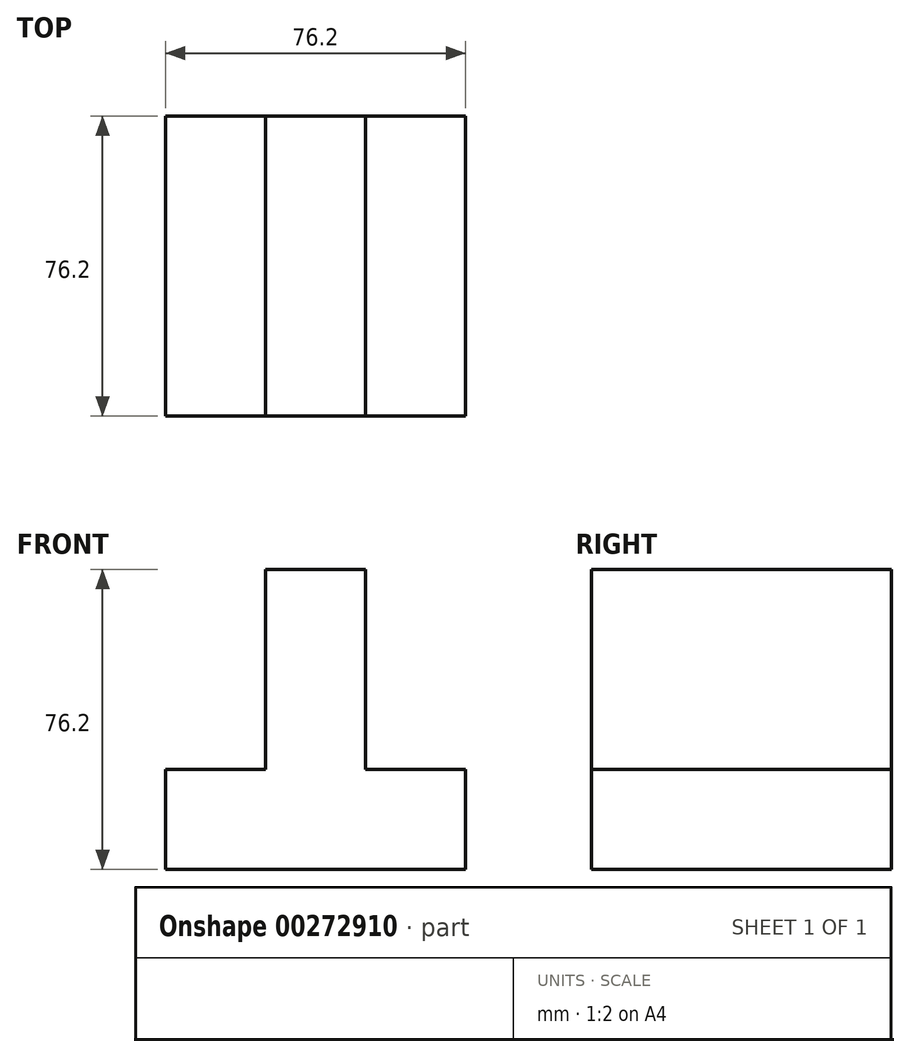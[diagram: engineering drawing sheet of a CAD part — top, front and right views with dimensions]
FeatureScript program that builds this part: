
annotation { "Feature Type Name" : "Feature", "Feature Type Description" : "" }
export const myFeature = defineFeature(function(context is Context, id is Id, definition is map)
    precondition{}
    {
        {
            var Q0;
            Q0=qCreatedBy(makeId("Front.planeOp"),FACE);
            var sketch = newSketch(context, id + "F0", { "sketchPlane" : qUnion([Q0])});
            skLineSegment(sketch, "E0", {"start": v(0, 0) * mm, "end": v(-76.2, 0) * mm});
            skLineSegment(sketch, "E1", {"start": v(-76.2, 0) * mm, "end": v(-76.2, 25.4) * mm});
            skLineSegment(sketch, "E2", {"start": v(-76.2, 25.4) * mm, "end": v(-50.8, 25.4) * mm});
            skLineSegment(sketch, "E3", {"start": v(-50.8, 25.4) * mm, "end": v(-50.8, 76.2) * mm});
            skLineSegment(sketch, "E4", {"start": v(-50.8, 76.2) * mm, "end": v(-25.4, 76.2) * mm});
            skLineSegment(sketch, "E5", {"start": v(-25.4, 76.2) * mm, "end": v(-25.4, 25.4) * mm});
            skLineSegment(sketch, "E6", {"start": v(-25.4, 25.4) * mm, "end": v(0, 25.4) * mm});
            skLineSegment(sketch, "E7", {"start": v(0, 25.4) * mm, "end": v(0, 0) * mm});
            skSolve(sketch);
        }
        {
            var Q0;
            Q0 = qSketchRegion(id + "F0", true);
            extrude(context, id + "F1", {"entities" : qUnion([Q0]), "depth" : 76.2 * mm});
        }
    });
